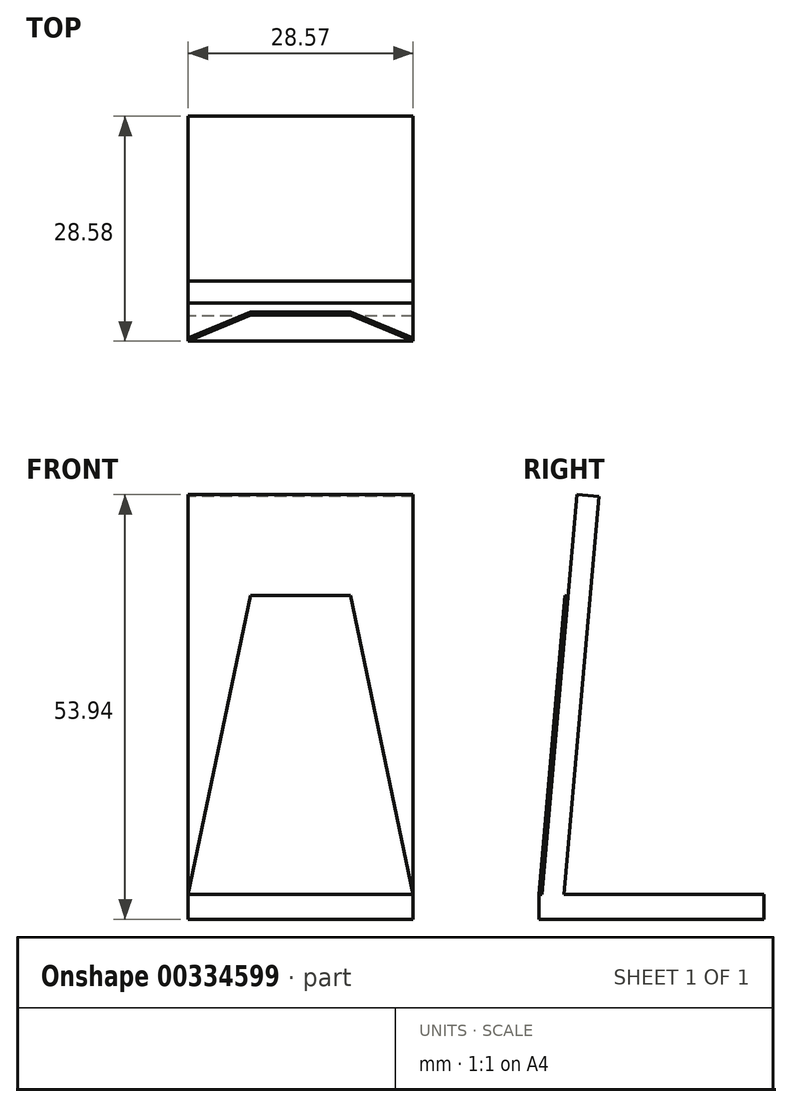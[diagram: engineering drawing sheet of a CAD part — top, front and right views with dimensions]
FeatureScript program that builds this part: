
annotation { "Feature Type Name" : "Feature", "Feature Type Description" : "" }
export const myFeature = defineFeature(function(context is Context, id is Id, definition is map)
    precondition{}
    {
        {
            var Q0;
            Q0=qCreatedBy(makeId("Right.planeOp"),FACE);
            var sketch = newSketch(context, id + "F0", { "sketchPlane" : qUnion([Q0])});
            skLineSegment(sketch, "E0", {"start": v(-14.29, 0) * mm, "end": v(14.29, 0) * mm});
            skLineSegment(sketch, "E1", {"start": v(14.29, 0) * mm, "end": v(14.29, 3.17) * mm});
            skLineSegment(sketch, "E2", {"start": v(14.29, 3.17) * mm, "end": v(-14.29, 3.17) * mm});
            skLineSegment(sketch, "E3", {"start": v(-14.29, 3.17) * mm, "end": v(-14.29, 0) * mm});
            skLineSegment(sketch, "E4", {"start": v(-5.01, 3.17) * mm, "end": v(-5.01, 53.98) * mm, "construction": true});
            skLineSegment(sketch, "E5", {"start": v(-14.29, 3.18) * mm, "end": v(-9.84, 53.97) * mm});
            skLineSegment(sketch, "E6", {"start": v(-9.84, 53.98) * mm, "end": v(-6.68, 53.7) * mm});
            skLineSegment(sketch, "E7", {"start": v(-6.68, 53.7) * mm, "end": v(-11.1, 3.18) * mm});
            skLineSegment(sketch, "E8", {"start": v(-11.1, 3.17) * mm, "end": v(-14.29, 3.17) * mm});
            skSolve(sketch);
        }
        {
            var Q0;
            Q0 = qSketchRegion(id + "F0", true);
            extrude(context, id + "F1", {"entities" : qUnion([Q0]), "depth" : 28.57 * mm});
        }
        {
            var Q0;
            Q0=makeQuery(id+"F1.opExtrude","SWEPT_FACE",FACE,{"disambiguationData":[OSD([sQuery(id+"F0.wireOp",EDGE,"E5")])]});
            var sketch = newSketch(context, id + "F2", { "sketchPlane" : qUnion([Q0])});
            skLineSegment(sketch, "E9", {"start": v(14.29, 1.92) * mm, "end": v(14.29, 40.02) * mm, "construction": true});
            skLineSegment(sketch, "E10", {"start": v(7.94, 40.02) * mm, "end": v(20.64, 40.02) * mm});
            skLineSegment(sketch, "E11", {"start": v(7.94, 40.02) * mm, "end": v(0, 1.92) * mm});
            skLineSegment(sketch, "E12", {"start": v(0, 1.92) * mm, "end": v(28.58, 1.92) * mm});
            skLineSegment(sketch, "E13", {"start": v(28.58, 1.92) * mm, "end": v(20.64, 40.02) * mm});
            skSolve(sketch);
        }
        {
            var Q0;
            Q0=makeQuery(id+"F2.imprint","IMPRINT",FACE,{"disambiguationData":[TD([[makeQuery(id+"F2.imprint","IMPRINT",EDGE,{"derivedFrom":sQuery(id+"F2.wireOp",EDGE,"E10")}),1.0]])]});
            extrude(context, id + "F3", {"entities" : qUnion([Q0]), "operationType" : NewBodyOperationType.REMOVE, "oppositeDirection" : true, "depth" : 0.38 * mm});
        }
    });
